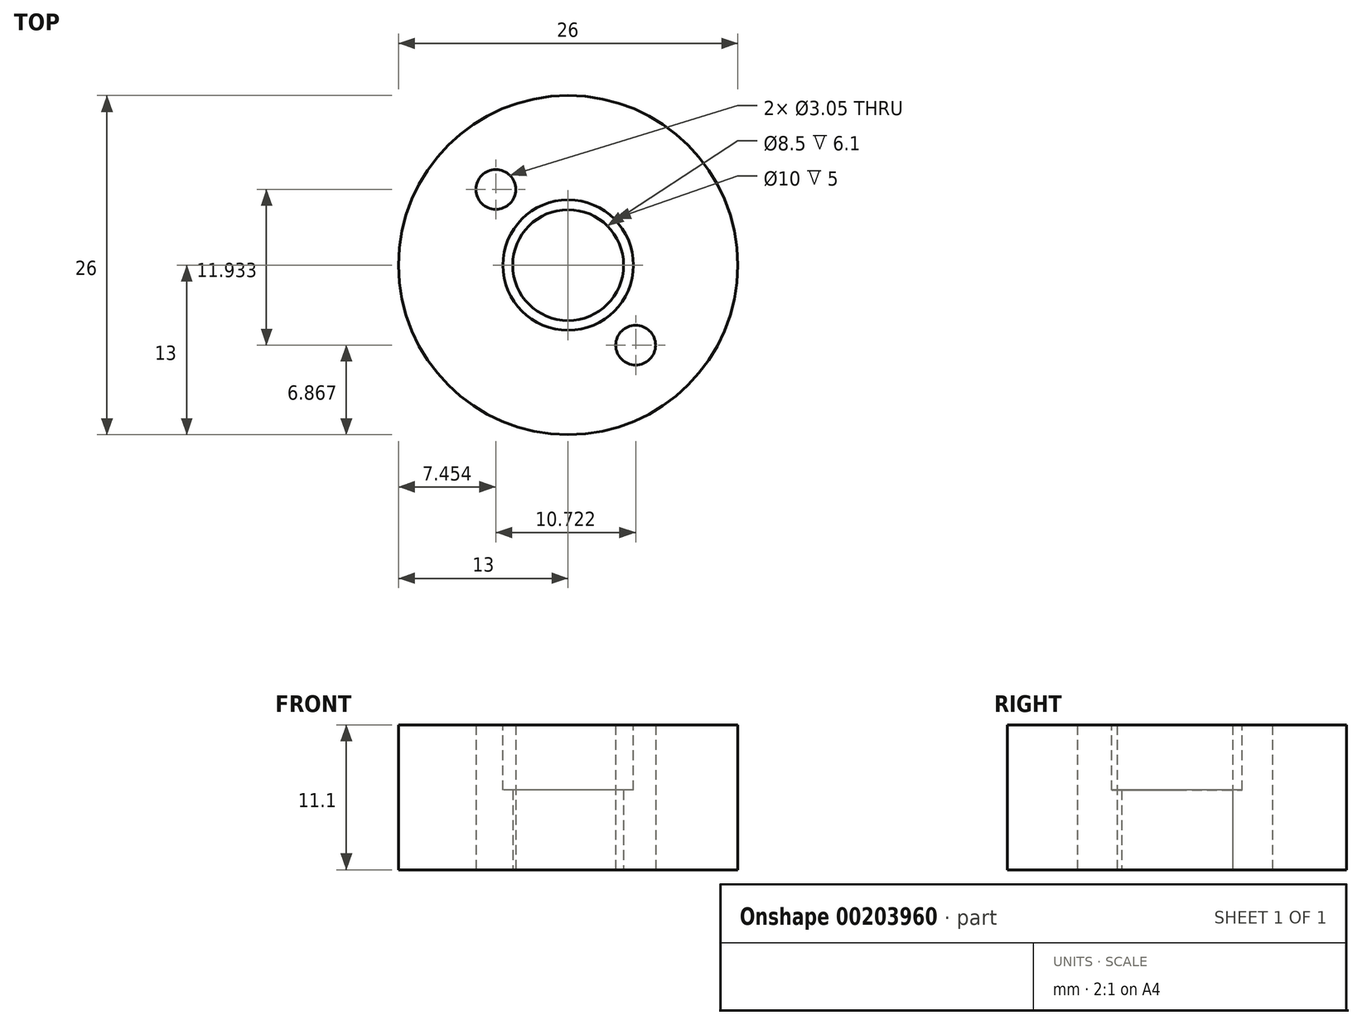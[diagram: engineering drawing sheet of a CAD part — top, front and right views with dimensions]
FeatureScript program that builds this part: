
annotation { "Feature Type Name" : "Feature", "Feature Type Description" : "" }
export const myFeature = defineFeature(function(context is Context, id is Id, definition is map)
    precondition{}
    {
        {
            var Q0;
            Q0=qCreatedBy(makeId("Top.planeOp"),FACE);
            var sketch = newSketch(context, id + "F0", { "sketchPlane" : qUnion([Q0])});
            skCircle(sketch, "E0", {"center": v(0, 0) * mm, "radius": 4.25 * mm});
            skCircle(sketch, "E1", {"center": v(0, 0) * mm, "radius": 13 * mm});
            skCircle(sketch, "E2", {"center": v(-5.55, 5.8) * mm, "radius": 1.52 * mm});
            skCircle(sketch, "E3", {"center": v(5.18, -6.13) * mm, "radius": 1.52 * mm});
            skSolve(sketch);
        }
        {
            var Q0;
            Q0=makeQuery(id+"F0.imprint","IMPRINT",FACE,{"disambiguationData":[TD([[makeQuery(id+"F0.imprint","IMPRINT",EDGE,{"derivedFrom":sQuery(id+"F0.wireOp",EDGE,"E0")}),-1.0]])]});
            extrude(context, id + "F1", {"entities" : qUnion([Q0]), "depth" : 11.1 * mm});
        }
        {
            var Q0;
            Q0=makeQuery(id+"F1.opExtrude","CAP_FACE",FACE,{"disambiguationData":[OSD([sQuery(id+"F0.wireOp",EDGE,"E0"),sQuery(id+"F0.wireOp",EDGE,"E1"),sQuery(id+"F0.wireOp",EDGE,"E2"),sQuery(id+"F0.wireOp",EDGE,"E3")])],"isStart":false});
            var sketch = newSketch(context, id + "F2", { "sketchPlane" : qUnion([Q0])});
            skCircle(sketch, "E4", {"center": v(0, 0) * mm, "radius": 5 * mm});
            skSolve(sketch);
        }
        {
            var Q0;
            Q0=makeQuery(id+"F2.imprint","IMPRINT",FACE,{"disambiguationData":[TD([[makeQuery(id+"F2.imprint","IMPRINT",EDGE,{"derivedFrom":sQuery(id+"F2.wireOp",EDGE,"E4")}),1.0]])]});
            extrude(context, id + "F3", {"entities" : qUnion([Q0]), "operationType" : NewBodyOperationType.REMOVE, "oppositeDirection" : true, "depth" : 5 * mm});
        }
    });
